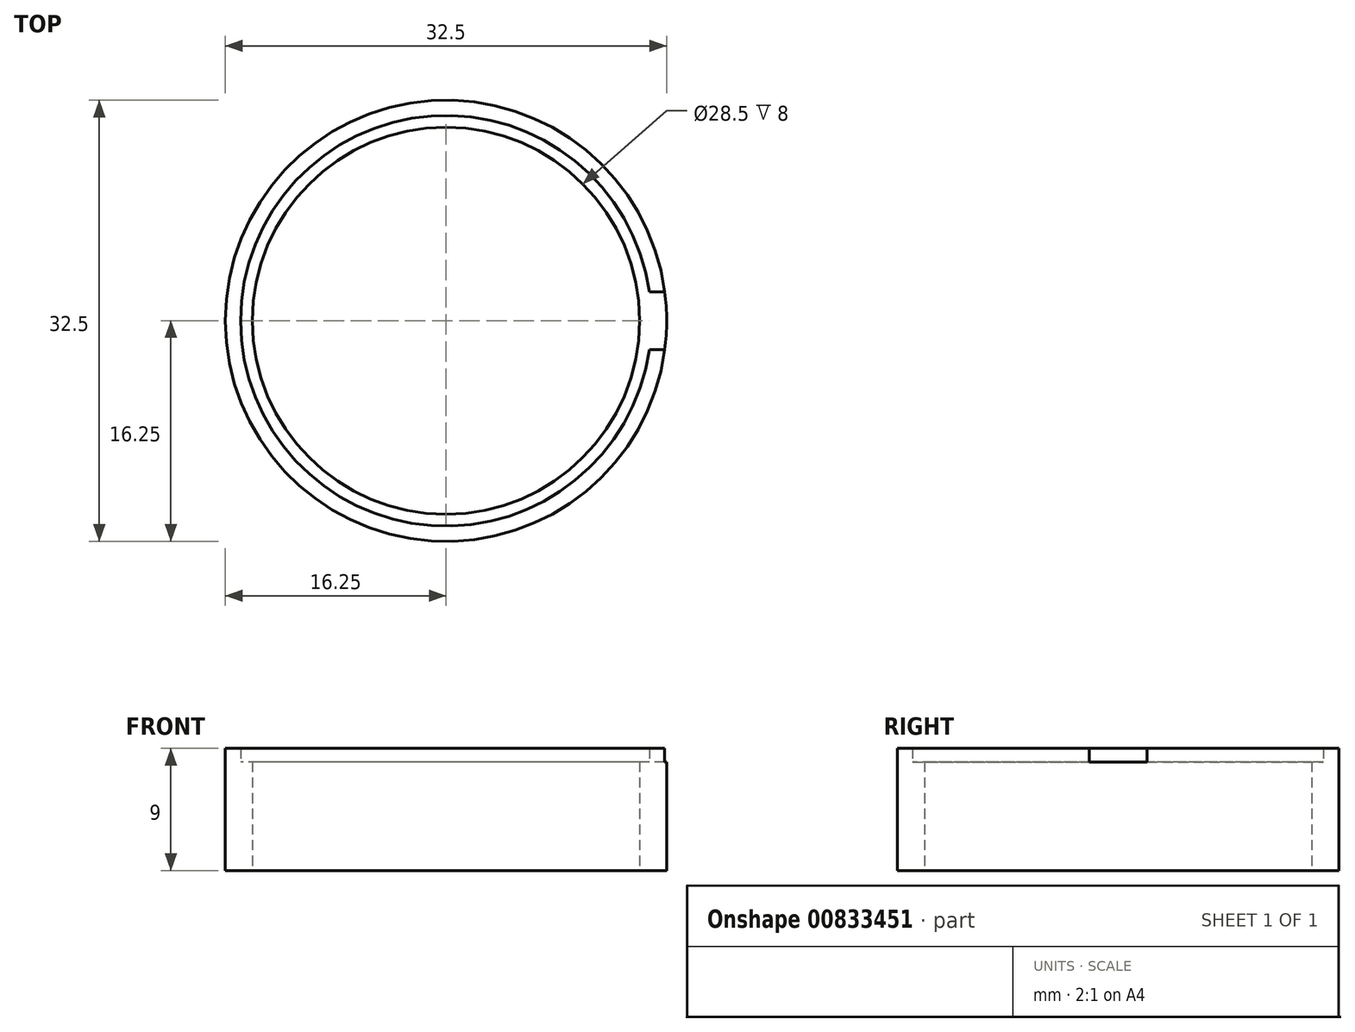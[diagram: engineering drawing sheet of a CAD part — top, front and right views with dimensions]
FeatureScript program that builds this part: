
annotation { "Feature Type Name" : "Feature", "Feature Type Description" : "" }
export const myFeature = defineFeature(function(context is Context, id is Id, definition is map)
    precondition{}
    {
        {
            var Q0;
            Q0=qCreatedBy(makeId("Top.planeOp"),FACE);
            var sketch = newSketch(context, id + "F0", { "sketchPlane" : qUnion([Q0])});
            skCircle(sketch, "E0", {"center": v(0, 0) * mm, "radius": 16.25 * mm});
            skCircle(sketch, "E1", {"center": v(0, 0) * mm, "radius": 14.25 * mm});
            skSolve(sketch);
        }
        {
            var Q0;
            Q0 = qSketchRegion(id + "F0", true);
            extrude(context, id + "F1", {"entities" : qUnion([Q0]), "depth" : 7.25 * mm, "offsetDistance" : 25 * mm, "hasSecondDirection" : true, "secondDirectionOppositeDirection" : true, "secondDirectionDepth" : .75 * mm});
        }
        {
            var Q0;
            Q0=makeQuery(id+"F1.opExtrude","CAP_FACE",FACE,{"disambiguationData":[OSD([sQuery(id+"F0.wireOp",EDGE,"E0"),sQuery(id+"F0.wireOp",EDGE,"E1")])],"isStart":false});
            var sketch = newSketch(context, id + "F2", { "sketchPlane" : qUnion([Q0])});
            skCircle(sketch, "E2", {"center": v(0, 0) * mm, "radius": 15.12 * mm});
            skCircle(sketch, "E3", {"center": v(0, 0) * mm, "radius": 16.25 * mm});
            skSolve(sketch);
        }
        {
            var Q0;
            Q0 = qSketchRegion(id + "F2", true);
            extrude(context, id + "F3", {"entities" : qUnion([Q0]), "operationType" : NewBodyOperationType.ADD, "depth" : 1 * mm, "offsetDistance" : 25 * mm});
        }
        {
            var Q0;
            Q0=makeQuery(id+"F3.opExtrude","CAP_FACE",FACE,{"disambiguationData":[OSD([sQuery(id+"F2.wireOp",EDGE,"E2"),sQuery(id+"F2.wireOp",EDGE,"E3")])],"isStart":false});
            var sketch = newSketch(context, id + "F4", { "sketchPlane" : qUnion([Q0])});
            skLineSegment(sketch, "E4.bottom", {"start": v(17.12, -2.13) * mm, "end": v(13.12, -2.13) * mm});
            skLineSegment(sketch, "E4.top", {"start": v(17.12, 2.12) * mm, "end": v(13.12, 2.12) * mm});
            skLineSegment(sketch, "E4.left", {"start": v(17.12, -2.13) * mm, "end": v(17.12, 2.12) * mm});
            skLineSegment(sketch, "E4.right", {"start": v(13.12, -2.13) * mm, "end": v(13.12, 2.12) * mm});
            skPoint(sketch, "E4.middle", {"position": v(15.12, 0) * mm});
            skSolve(sketch);
        }
        {
            var Q0;
            Q0 = qSketchRegion(id + "F4", true);
            extrude(context, id + "F5", {"entities" : qUnion([Q0]), "operationType" : NewBodyOperationType.REMOVE, "oppositeDirection" : true, "depth" : 1 * mm, "offsetDistance" : 25 * mm});
        }
    });
